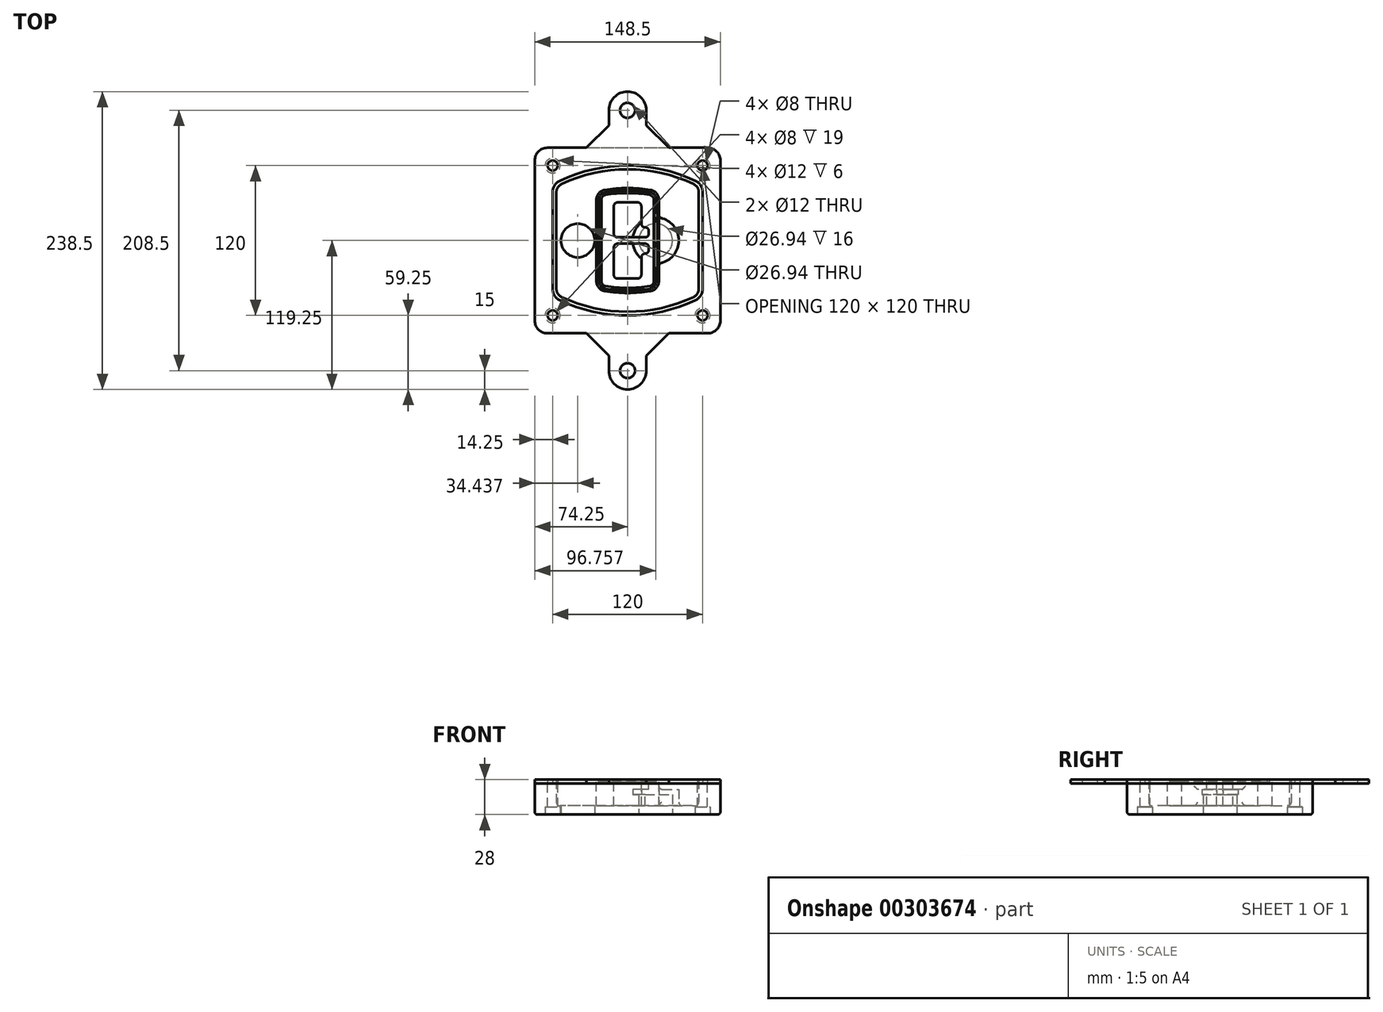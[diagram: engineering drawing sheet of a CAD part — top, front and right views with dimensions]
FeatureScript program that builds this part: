
annotation { "Feature Type Name" : "Feature", "Feature Type Description" : "" }
export const myFeature = defineFeature(function(context is Context, id is Id, definition is map)
    precondition{}
    {
        {
            var Q0;
            Q0=qCreatedBy(makeId("Top.planeOp"),FACE);
            var sketch = newSketch(context, id + "F0", { "sketchPlane" : qUnion([Q0])});
            skPoint(sketch, "E0.rect.middle", {"position": v(0, 0) * mm});
            skLineSegment(sketch, "E1.bottom", {"start": v(-64.25, -74.25) * mm, "end": v(64.25, -74.25) * mm});
            skLineSegment(sketch, "E1.top", {"start": v(-64.25, 74.25) * mm, "end": v(64.25, 74.25) * mm});
            skLineSegment(sketch, "E1.left", {"start": v(-74.25, -64.25) * mm, "end": v(-74.25, 64.25) * mm});
            skLineSegment(sketch, "E1.right", {"start": v(74.25, -64.25) * mm, "end": v(74.25, 64.25) * mm});
            skLineSegment(sketch, "E2", {"start": v(-74.25, 74.25) * mm, "end": v(74.25, -74.25) * mm, "construction": true});
            skLineSegment(sketch, "E3", {"start": v(74.25, 74.25) * mm, "end": v(-74.25, -74.25) * mm, "construction": true});
            skCircle(sketch, "E4", {"center": v(-60, 60) * mm, "radius": 4 * mm});
            skCircle(sketch, "E5", {"center": v(60, 60) * mm, "radius": 4 * mm});
            skCircle(sketch, "E6", {"center": v(60, -60) * mm, "radius": 4 * mm});
            skCircle(sketch, "E7", {"center": v(-60, -60) * mm, "radius": 4 * mm});
            skLineSegment(sketch, "E8", {"start": v(-60, 60) * mm, "end": v(60, 60) * mm, "construction": true});
            skLineSegment(sketch, "E9", {"start": v(60, 60) * mm, "end": v(60, -60) * mm, "construction": true});
            skLineSegment(sketch, "E10", {"start": v(60, -60) * mm, "end": v(-60, -60) * mm, "construction": true});
            skLineSegment(sketch, "E11", {"start": v(-60, -60) * mm, "end": v(-60, 60) * mm, "construction": true});
            skLineSegment(sketch, "E12", {"start": v(-60, 38.83) * mm, "end": v(-60, -38.83) * mm});
            skLineSegment(sketch, "E13", {"start": v(60, 38.83) * mm, "end": v(60, -38.83) * mm});
            skArc(sketch, "E14", {"start": v(54.26, 47.88) * mm, "mid": v(0, 60) * mm, "end": v(-54.26, 47.88) * mm});
            skArc(sketch, "E15", {"start": v(-54.26, -47.88) * mm, "mid": v(0, -60) * mm, "end": v(54.26, -47.88) * mm});
            skLineSegment(sketch, "E16", {"start": v(-60, 0) * mm, "end": v(60, 0) * mm, "construction": true});
            skPoint(sketch, "E17.visualSharp", {"position": v(-60, -45) * mm});
            skArc(sketch, "E17.filletArc", {"start": v(-60, -38.83) * mm, "mid": v(-58.44, -44.2) * mm, "end": v(-54.26, -47.88) * mm});
            skPoint(sketch, "E18.visualSharp", {"position": v(-60, 45) * mm});
            skArc(sketch, "E18.filletArc", {"start": v(-54.26, 47.88) * mm, "mid": v(-58.44, 44.2) * mm, "end": v(-60, 38.83) * mm});
            skPoint(sketch, "E19.visualSharp", {"position": v(60, 45) * mm});
            skArc(sketch, "E19.filletArc", {"start": v(60, 38.83) * mm, "mid": v(58.44, 44.2) * mm, "end": v(54.26, 47.88) * mm});
            skPoint(sketch, "E20.visualSharp", {"position": v(60, -45) * mm});
            skArc(sketch, "E20.filletArc", {"start": v(54.26, -47.88) * mm, "mid": v(58.44, -44.2) * mm, "end": v(60, -38.83) * mm});
            skPoint(sketch, "E21.visualSharp", {"position": v(-74.25, 74.25) * mm});
            skArc(sketch, "E21.filletArc", {"start": v(-64.25, 74.25) * mm, "mid": v(-71.32, 71.32) * mm, "end": v(-74.25, 64.25) * mm});
            skPoint(sketch, "E22.visualSharp", {"position": v(74.25, 74.25) * mm});
            skArc(sketch, "E22.filletArc", {"start": v(74.25, 64.25) * mm, "mid": v(71.32, 71.32) * mm, "end": v(64.25, 74.25) * mm});
            skPoint(sketch, "E23.visualSharp", {"position": v(74.25, -74.25) * mm});
            skArc(sketch, "E23.filletArc", {"start": v(64.25, -74.25) * mm, "mid": v(71.32, -71.32) * mm, "end": v(74.25, -64.25) * mm});
            skPoint(sketch, "E24.visualSharp", {"position": v(-74.25, -74.25) * mm});
            skArc(sketch, "E24.filletArc", {"start": v(-74.25, -64.25) * mm, "mid": v(-71.32, -71.32) * mm, "end": v(-64.25, -74.25) * mm});
            skArc(sketch, "E25.0", {"start": v(57, 38.83) * mm, "mid": v(55.9, 42.58) * mm, "end": v(52.98, 45.17) * mm});
            skLineSegment(sketch, "E25.1", {"start": v(57, 38.83) * mm, "end": v(57, -38.83) * mm});
            skArc(sketch, "E25.2", {"start": v(52.98, -45.17) * mm, "mid": v(55.9, -42.58) * mm, "end": v(57, -38.83) * mm});
            skArc(sketch, "E25.3", {"start": v(-52.98, -45.17) * mm, "mid": v(0, -57) * mm, "end": v(52.98, -45.17) * mm});
            skArc(sketch, "E25.4", {"start": v(-57, -38.83) * mm, "mid": v(-55.9, -42.58) * mm, "end": v(-52.98, -45.17) * mm});
            skArc(sketch, "E25.5", {"start": v(52.98, 45.17) * mm, "mid": v(0, 57) * mm, "end": v(-52.98, 45.17) * mm});
            skLineSegment(sketch, "E25.6", {"start": v(-57, 38.83) * mm, "end": v(-57, -38.83) * mm});
            skArc(sketch, "E25.7", {"start": v(-52.98, 45.17) * mm, "mid": v(-55.9, 42.58) * mm, "end": v(-57, 38.83) * mm});
            skArc(sketch, "E26.0", {"start": v(-55.96, 51.5) * mm, "mid": v(-61.82, 46.33) * mm, "end": v(-64, 38.83) * mm});
            skArc(sketch, "E26.1", {"start": v(55.96, 51.5) * mm, "mid": v(0, 64) * mm, "end": v(-55.96, 51.5) * mm});
            skArc(sketch, "E26.2", {"start": v(64, 38.83) * mm, "mid": v(61.82, 46.33) * mm, "end": v(55.96, 51.5) * mm});
            skLineSegment(sketch, "E26.3", {"start": v(64, 38.83) * mm, "end": v(64, -38.83) * mm});
            skArc(sketch, "E26.4", {"start": v(55.96, -51.5) * mm, "mid": v(61.82, -46.33) * mm, "end": v(64, -38.83) * mm});
            skLineSegment(sketch, "E26.5", {"start": v(-64, 38.83) * mm, "end": v(-64, -38.83) * mm});
            skArc(sketch, "E26.6", {"start": v(-55.96, -51.5) * mm, "mid": v(0, -64) * mm, "end": v(55.96, -51.5) * mm});
            skArc(sketch, "E26.7", {"start": v(-64, -38.83) * mm, "mid": v(-61.82, -46.33) * mm, "end": v(-55.96, -51.5) * mm});
            skSolve(sketch);
        }
        {
            var Q0;
            Q0=makeQuery(id+"F0.imprint","IMPRINT",FACE,{"disambiguationData":[TD([[makeQuery(id+"F0.imprint","IMPRINT",EDGE,{"derivedFrom":sQuery(id+"F0.wireOp",EDGE,"E1.bottom")}),1.0]])]});
            var Q1;
            Q1=makeQuery(id+"F0.imprint","IMPRINT",FACE,{"disambiguationData":[TD([[makeQuery(id+"F0.imprint","IMPRINT",EDGE,{"derivedFrom":sQuery(id+"F0.wireOp",EDGE,"E12")}),1.0]])]});
            var Q2;
            Q2=makeQuery(id+"F0.imprint","IMPRINT",FACE,{"disambiguationData":[TD([[makeQuery(id+"F0.imprint","IMPRINT",EDGE,{"derivedFrom":sQuery(id+"F0.wireOp",EDGE,"E25.0")}),1.0]])]});
            var Q3;
            Q3=makeQuery(id+"F0.imprint","IMPRINT",FACE,{"disambiguationData":[TD([[makeQuery(id+"F0.imprint","IMPRINT",EDGE,{"derivedFrom":sQuery(id+"F0.wireOp",EDGE,"E12")}),-1.0]])]});
            extrude(context, id + "F1", {"entities" : qUnion([Q0, Q1, Q2, Q3]), "oppositeDirection" : true, "depth" : 25 * mm});
        }
        {
            var Q0;
            Q0=makeQuery(id+"F0.imprint","IMPRINT",FACE,{"disambiguationData":[TD([[makeQuery(id+"F0.imprint","IMPRINT",EDGE,{"derivedFrom":sQuery(id+"F0.wireOp",EDGE,"E12")}),1.0]])]});
            extrude(context, id + "F2", {"entities" : qUnion([Q0]), "operationType" : NewBodyOperationType.ADD, "depth" : 3 * mm});
        }
        {
            var Q0;
            Q0=makeQuery(id+"F0.imprint","IMPRINT",FACE,{"disambiguationData":[TD([[makeQuery(id+"F0.imprint","IMPRINT",EDGE,{"derivedFrom":sQuery(id+"F0.wireOp",EDGE,"E25.0")}),1.0]])]});
            extrude(context, id + "F3", {"entities" : qUnion([Q0]), "operationType" : NewBodyOperationType.REMOVE, "oppositeDirection" : true, "depth" : 18 * mm});
        }
        {
            var Q0;
            Q0=makeQuery(id+"F2.opExtrude","CAP_FACE",FACE,{"disambiguationData":[OSD([sQuery(id+"F0.wireOp",EDGE,"E12"),sQuery(id+"F0.wireOp",EDGE,"E13"),sQuery(id+"F0.wireOp",EDGE,"E14"),sQuery(id+"F0.wireOp",EDGE,"E15"),sQuery(id+"F0.wireOp",EDGE,"E17.filletArc"),sQuery(id+"F0.wireOp",EDGE,"E18.filletArc"),sQuery(id+"F0.wireOp",EDGE,"E19.filletArc"),sQuery(id+"F0.wireOp",EDGE,"E20.filletArc"),sQuery(id+"F0.wireOp",EDGE,"E25.0"),sQuery(id+"F0.wireOp",EDGE,"E25.1"),sQuery(id+"F0.wireOp",EDGE,"E25.2"),sQuery(id+"F0.wireOp",EDGE,"E25.3"),sQuery(id+"F0.wireOp",EDGE,"E25.4"),sQuery(id+"F0.wireOp",EDGE,"E25.5"),sQuery(id+"F0.wireOp",EDGE,"E25.6"),sQuery(id+"F0.wireOp",EDGE,"E25.7")])],"isStart":false});
            var sketch = newSketch(context, id + "F4", { "sketchPlane" : qUnion([Q0])});
            skArc(sketch, "E27.0", {"start": v(-18.34, -40.45) * mm, "mid": v(0, -42) * mm, "end": v(18.34, -40.45) * mm});
            skArc(sketch, "E28.0", {"start": v(18.34, 40.45) * mm, "mid": v(0, 42) * mm, "end": v(-18.34, 40.45) * mm});
            skLineSegment(sketch, "E29", {"start": v(-25, 32.57) * mm, "end": v(-25, -32.57) * mm});
            skLineSegment(sketch, "E30", {"start": v(25, 32.57) * mm, "end": v(25, -32.57) * mm});
            skLineSegment(sketch, "E31", {"start": v(-25, 39.1) * mm, "end": v(25, 39.1) * mm, "construction": true});
            skLineSegment(sketch, "E32", {"start": v(-25, -39.1) * mm, "end": v(25, -39.1) * mm, "construction": true});
            skPoint(sketch, "E33.visualSharp", {"position": v(-25, 39.1) * mm});
            skArc(sketch, "E33.filletArc", {"start": v(-18.34, 40.45) * mm, "mid": v(-23.11, 37.73) * mm, "end": v(-25, 32.57) * mm});
            skPoint(sketch, "E34.visualSharp", {"position": v(25, 39.1) * mm});
            skArc(sketch, "E34.filletArc", {"start": v(25, 32.57) * mm, "mid": v(23.11, 37.73) * mm, "end": v(18.34, 40.45) * mm});
            skPoint(sketch, "E35.visualSharp", {"position": v(25, -39.1) * mm});
            skArc(sketch, "E35.filletArc", {"start": v(18.34, -40.45) * mm, "mid": v(23.11, -37.73) * mm, "end": v(25, -32.57) * mm});
            skPoint(sketch, "E36.visualSharp", {"position": v(-25, -39.1) * mm});
            skArc(sketch, "E36.filletArc", {"start": v(-25, -32.57) * mm, "mid": v(-23.11, -37.73) * mm, "end": v(-18.34, -40.45) * mm});
            skArc(sketch, "E37.0", {"start": v(52.98, 45.17) * mm, "mid": v(0, 57) * mm, "end": v(-52.98, 45.17) * mm});
            skArc(sketch, "E37.1", {"start": v(-52.98, 45.17) * mm, "mid": v(-55.9, 42.58) * mm, "end": v(-57, 38.83) * mm});
            skLineSegment(sketch, "E37.2", {"start": v(-57, 38.83) * mm, "end": v(-57, -38.83) * mm});
            skArc(sketch, "E37.3", {"start": v(-57, -38.83) * mm, "mid": v(-55.9, -42.58) * mm, "end": v(-52.98, -45.17) * mm});
            skArc(sketch, "E37.4", {"start": v(-52.98, -45.17) * mm, "mid": v(0, -57) * mm, "end": v(52.98, -45.17) * mm});
            skArc(sketch, "E37.5", {"start": v(52.98, -45.17) * mm, "mid": v(55.9, -42.58) * mm, "end": v(57, -38.83) * mm});
            skLineSegment(sketch, "E37.6", {"start": v(57, 38.83) * mm, "end": v(57, -38.83) * mm});
            skArc(sketch, "E37.7", {"start": v(57, 38.83) * mm, "mid": v(55.9, 42.58) * mm, "end": v(52.98, 45.17) * mm});
            skLineSegment(sketch, "E38.0", {"start": v(23, 32.57) * mm, "end": v(23, -32.57) * mm});
            skArc(sketch, "E38.1", {"start": v(18, -38.48) * mm, "mid": v(21.58, -36.44) * mm, "end": v(23, -32.57) * mm});
            skArc(sketch, "E38.2", {"start": v(-18, -38.48) * mm, "mid": v(0, -40) * mm, "end": v(18, -38.48) * mm});
            skArc(sketch, "E38.3", {"start": v(-23, -32.57) * mm, "mid": v(-21.58, -36.44) * mm, "end": v(-18, -38.48) * mm});
            skLineSegment(sketch, "E38.4", {"start": v(-23, 32.57) * mm, "end": v(-23, -32.57) * mm});
            skArc(sketch, "E38.5", {"start": v(23, 32.57) * mm, "mid": v(21.58, 36.44) * mm, "end": v(18, 38.48) * mm});
            skArc(sketch, "E38.6", {"start": v(-18, 38.48) * mm, "mid": v(-21.58, 36.44) * mm, "end": v(-23, 32.57) * mm});
            skArc(sketch, "E38.7", {"start": v(18, 38.48) * mm, "mid": v(0, 40) * mm, "end": v(-18, 38.48) * mm});
            skArc(sketch, "E39.0", {"start": v(21, 32.57) * mm, "mid": v(20.06, 35.15) * mm, "end": v(17.67, 36.5) * mm});
            skLineSegment(sketch, "E39.1", {"start": v(21, 32.57) * mm, "end": v(21, -32.57) * mm});
            skArc(sketch, "E39.2", {"start": v(17.67, -36.5) * mm, "mid": v(20.06, -35.15) * mm, "end": v(21, -32.57) * mm});
            skArc(sketch, "E39.3", {"start": v(-17.67, -36.5) * mm, "mid": v(0, -38) * mm, "end": v(17.67, -36.5) * mm});
            skArc(sketch, "E39.4", {"start": v(-21, -32.57) * mm, "mid": v(-20.06, -35.15) * mm, "end": v(-17.67, -36.5) * mm});
            skArc(sketch, "E39.5", {"start": v(17.67, 36.5) * mm, "mid": v(0, 38) * mm, "end": v(-17.67, 36.5) * mm});
            skLineSegment(sketch, "E39.6", {"start": v(-21, 32.57) * mm, "end": v(-21, -32.57) * mm});
            skArc(sketch, "E39.7", {"start": v(-17.67, 36.5) * mm, "mid": v(-20.06, 35.15) * mm, "end": v(-21, 32.57) * mm});
            skLineSegment(sketch, "E40", {"start": v(-25, 0) * mm, "end": v(25, 0) * mm, "construction": true});
            skLineSegment(sketch, "E41", {"start": v(-11, 5.5) * mm, "end": v(-11, 27.5) * mm});
            skLineSegment(sketch, "E42", {"start": v(-8, 30.5) * mm, "end": v(8, 30.5) * mm});
            skLineSegment(sketch, "E43", {"start": v(11, 27.5) * mm, "end": v(11, 13.5) * mm});
            skLineSegment(sketch, "E44", {"start": v(14, 10.5) * mm, "end": v(14, 10.5) * mm});
            skLineSegment(sketch, "E45", {"start": v(17, 7.5) * mm, "end": v(17, 5.5) * mm});
            skLineSegment(sketch, "E46", {"start": v(14, 2.5) * mm, "end": v(-8, 2.5) * mm});
            skPoint(sketch, "E47.visualSharp", {"position": v(-11, 30.5) * mm});
            skArc(sketch, "E47.filletArc", {"start": v(-8, 30.5) * mm, "mid": v(-10.12, 29.62) * mm, "end": v(-11, 27.5) * mm});
            skPoint(sketch, "E48.visualSharp", {"position": v(11, 30.5) * mm});
            skArc(sketch, "E48.filletArc", {"start": v(11, 27.5) * mm, "mid": v(10.12, 29.62) * mm, "end": v(8, 30.5) * mm});
            skPoint(sketch, "E49.visualSharp", {"position": v(11, 10.5) * mm});
            skArc(sketch, "E49.filletArc", {"start": v(11, 13.5) * mm, "mid": v(11.88, 11.38) * mm, "end": v(14, 10.5) * mm});
            skPoint(sketch, "E50.visualSharp", {"position": v(17, 10.5) * mm});
            skArc(sketch, "E50.filletArc", {"start": v(17, 7.5) * mm, "mid": v(16.12, 9.62) * mm, "end": v(14, 10.5) * mm});
            skPoint(sketch, "E51.visualSharp", {"position": v(17, 2.5) * mm});
            skArc(sketch, "E51.filletArc", {"start": v(14, 2.5) * mm, "mid": v(16.12, 3.38) * mm, "end": v(17, 5.5) * mm});
            skPoint(sketch, "E52.visualSharp", {"position": v(-11, 2.5) * mm});
            skArc(sketch, "E52.filletArc", {"start": v(-11, 5.5) * mm, "mid": v(-10.12, 3.38) * mm, "end": v(-8, 2.5) * mm});
            skLineSegment(sketch, "E53.0.MirrorCS", {"start": v(14, -2.5) * mm, "end": v(-8, -2.5) * mm});
            skArc(sketch, "E54.0.MirrorCS", {"start": v(-11, -5.5) * mm, "mid": v(-10.12, -3.38) * mm, "end": v(-8, -2.5) * mm});
            skLineSegment(sketch, "E55.0.MirrorCS", {"start": v(-11, -5.5) * mm, "end": v(-11, -27.5) * mm});
            skArc(sketch, "E56.0.MirrorCS", {"start": v(-8, -30.5) * mm, "mid": v(-10.12, -29.62) * mm, "end": v(-11, -27.5) * mm});
            skLineSegment(sketch, "E57.0.MirrorCS", {"start": v(-8, -30.5) * mm, "end": v(8, -30.5) * mm});
            skArc(sketch, "E58.0.MirrorCS", {"start": v(11, -27.5) * mm, "mid": v(10.12, -29.62) * mm, "end": v(8, -30.5) * mm});
            skLineSegment(sketch, "E59.0.MirrorCS", {"start": v(11, -27.5) * mm, "end": v(11, -13.5) * mm});
            skArc(sketch, "E60.0.MirrorCS", {"start": v(11, -13.5) * mm, "mid": v(11.88, -11.38) * mm, "end": v(14, -10.5) * mm});
            skArc(sketch, "E61.0.MirrorCS", {"start": v(17, -7.5) * mm, "mid": v(16.12, -9.62) * mm, "end": v(14, -10.5) * mm});
            skLineSegment(sketch, "E62.0.MirrorCS", {"start": v(17, -7.5) * mm, "end": v(17, -5.5) * mm});
            skArc(sketch, "E63.0.MirrorCS", {"start": v(14, -2.5) * mm, "mid": v(16.12, -3.38) * mm, "end": v(17, -5.5) * mm});
            skSolve(sketch);
        }
        {
            var Q0;
            Q0=makeQuery(id+"F4.imprint","IMPRINT",FACE,{"disambiguationData":[TD([[makeQuery(id+"F4.imprint","IMPRINT",EDGE,{"derivedFrom":sQuery(id+"F4.wireOp",EDGE,"E27.0")}),1.0]])]});
            var Q1;
            Q1=makeQuery(id+"F4.imprint","IMPRINT",FACE,{"disambiguationData":[TD([[makeQuery(id+"F4.imprint","IMPRINT",EDGE,{"derivedFrom":sQuery(id+"F4.wireOp",EDGE,"E38.0")}),-1.0]])]});
            var Q2;
            Q2=makeQuery(id+"F4.imprint","IMPRINT",FACE,{"disambiguationData":[TD([[makeQuery(id+"F4.imprint","IMPRINT",EDGE,{"derivedFrom":sQuery(id+"F4.wireOp",EDGE,"E39.0")}),1.0]])]});
            extrude(context, id + "F5", {"entities" : qUnion([Q0, Q1, Q2]), "operationType" : NewBodyOperationType.ADD, "endBound" : BoundingType.UP_TO_NEXT, "oppositeDirection" : true, "depth" : 25 * mm});
        }
        {
            var Q0;
            Q0=makeQuery(id+"F4.imprint","IMPRINT",FACE,{"disambiguationData":[TD([[makeQuery(id+"F4.imprint","IMPRINT",EDGE,{"derivedFrom":sQuery(id+"F4.wireOp",EDGE,"E38.0")}),-1.0]])]});
            extrude(context, id + "F6", {"entities" : qUnion([Q0]), "operationType" : NewBodyOperationType.REMOVE, "oppositeDirection" : true, "depth" : 2 * mm});
        }
        {
            var Q0;
            Q0=makeQuery(id+"F1.opExtrude","CAP_FACE",FACE,{"disambiguationData":[OSD([sQuery(id+"F0.wireOp",EDGE,"E1.bottom"),sQuery(id+"F0.wireOp",EDGE,"E1.top"),sQuery(id+"F0.wireOp",EDGE,"E1.left"),sQuery(id+"F0.wireOp",EDGE,"E1.right"),sQuery(id+"F0.wireOp",EDGE,"E4"),sQuery(id+"F0.wireOp",EDGE,"E5"),sQuery(id+"F0.wireOp",EDGE,"E6"),sQuery(id+"F0.wireOp",EDGE,"E7"),sQuery(id+"F0.wireOp",EDGE,"E21.filletArc"),sQuery(id+"F0.wireOp",EDGE,"E22.filletArc"),sQuery(id+"F0.wireOp",EDGE,"E23.filletArc"),sQuery(id+"F0.wireOp",EDGE,"E24.filletArc")])],"isStart":false});
            var sketch = newSketch(context, id + "F7", { "sketchPlane" : qUnion([Q0])});
            skCircle(sketch, "E64", {"center": v(22.5, 0) * mm, "radius": 13.47 * mm});
            skCircle(sketch, "E65", {"center": v(-39.81, 0) * mm, "radius": 13.47 * mm});
            skLineSegment(sketch, "E66", {"start": v(74.25, 0) * mm, "end": v(-74.25, 0) * mm});
            skCircle(sketch, "E67", {"center": v(22.5, 0) * mm, "radius": 18.47 * mm});
            skCircle(sketch, "E68", {"center": v(60, -60) * mm, "radius": 6 * mm});
            skCircle(sketch, "E69", {"center": v(-60, -60) * mm, "radius": 6 * mm});
            skCircle(sketch, "E70", {"center": v(-60, 60) * mm, "radius": 6 * mm});
            skCircle(sketch, "E71", {"center": v(60, 60) * mm, "radius": 6 * mm});
            skSolve(sketch);
        }
        {
            var Q0;
            {var subQ1=sQuery(id+"F7.wireOp",EDGE,"E66");var subQ4=sQuery(id+"F7.wireOp",EDGE,"E64");var subQ6=makeQuery(id+"F7.imprint","INTERSECT",VERTEX,{"disambiguationData":[OD(0.0)],"derivedFrom":[subQ4,subQ1]});Q0=makeQuery(id+"F7.imprint","IMPRINT",FACE,{"disambiguationData":[TD([[makeQuery(id+"F7.imprint","IMPRINT",EDGE,{"disambiguationData":[TD([[subQ6,-1.0]])],"derivedFrom":subQ4}),-1.0]])]});}
            var Q1;
            {var subQ0=sQuery(id+"F7.wireOp",EDGE,"E66");var subQ1=sQuery(id+"F7.wireOp",EDGE,"E64");var subQ3=makeQuery(id+"F7.imprint","INTERSECT",VERTEX,{"disambiguationData":[OD(0.0)],"derivedFrom":[subQ1,subQ0]});Q1=makeQuery(id+"F7.imprint","IMPRINT",FACE,{"disambiguationData":[TD([[makeQuery(id+"F7.imprint","IMPRINT",EDGE,{"disambiguationData":[TD([[subQ3,-1.0]])],"derivedFrom":subQ1}),1.0]])]});}
            var Q2;
            {var subQ0=sQuery(id+"F7.wireOp",EDGE,"E66");var subQ1=sQuery(id+"F7.wireOp",EDGE,"E64");var subQ3=makeQuery(id+"F7.imprint","INTERSECT",VERTEX,{"disambiguationData":[OD(0.0)],"derivedFrom":[subQ1,subQ0]});Q2=makeQuery(id+"F7.imprint","IMPRINT",FACE,{"disambiguationData":[TD([[makeQuery(id+"F7.imprint","IMPRINT",EDGE,{"disambiguationData":[TD([[subQ3,1.0]])],"derivedFrom":subQ1}),1.0]])]});}
            var Q3;
            {var subQ1=sQuery(id+"F7.wireOp",EDGE,"E66");var subQ4=sQuery(id+"F7.wireOp",EDGE,"E64");var subQ6=makeQuery(id+"F7.imprint","INTERSECT",VERTEX,{"disambiguationData":[OD(0.0)],"derivedFrom":[subQ4,subQ1]});Q3=makeQuery(id+"F7.imprint","IMPRINT",FACE,{"disambiguationData":[TD([[makeQuery(id+"F7.imprint","IMPRINT",EDGE,{"disambiguationData":[TD([[subQ6,1.0]])],"derivedFrom":subQ4}),-1.0]])]});}
            extrude(context, id + "F8", {"entities" : qUnion([Q0, Q1, Q2, Q3]), "operationType" : NewBodyOperationType.ADD, "oppositeDirection" : true, "depth" : 20 * mm});
        }
        {
            var Q0;
            {var subQ0=sQuery(id+"F7.wireOp",EDGE,"E66");var subQ1=sQuery(id+"F7.wireOp",EDGE,"E64");var subQ3=makeQuery(id+"F7.imprint","INTERSECT",VERTEX,{"disambiguationData":[OD(0.0)],"derivedFrom":[subQ1,subQ0]});Q0=makeQuery(id+"F7.imprint","IMPRINT",FACE,{"disambiguationData":[TD([[makeQuery(id+"F7.imprint","IMPRINT",EDGE,{"disambiguationData":[TD([[subQ3,-1.0]])],"derivedFrom":subQ1}),1.0]])]});}
            var Q1;
            {var subQ0=sQuery(id+"F7.wireOp",EDGE,"E66");var subQ1=sQuery(id+"F7.wireOp",EDGE,"E64");var subQ3=makeQuery(id+"F7.imprint","INTERSECT",VERTEX,{"disambiguationData":[OD(0.0)],"derivedFrom":[subQ1,subQ0]});Q1=makeQuery(id+"F7.imprint","IMPRINT",FACE,{"disambiguationData":[TD([[makeQuery(id+"F7.imprint","IMPRINT",EDGE,{"disambiguationData":[TD([[subQ3,1.0]])],"derivedFrom":subQ1}),1.0]])]});}
            extrude(context, id + "F9", {"entities" : qUnion([Q0, Q1]), "operationType" : NewBodyOperationType.REMOVE, "oppositeDirection" : true, "depth" : 16 * mm});
        }
        {
            var Q0;
            {var subQ0=sQuery(id+"F7.wireOp",EDGE,"E66");var subQ1=sQuery(id+"F7.wireOp",EDGE,"E65");var subQ3=makeQuery(id+"F7.imprint","INTERSECT",VERTEX,{"disambiguationData":[OD(0.0)],"derivedFrom":[subQ1,subQ0]});Q0=makeQuery(id+"F7.imprint","IMPRINT",FACE,{"disambiguationData":[TD([[makeQuery(id+"F7.imprint","IMPRINT",EDGE,{"disambiguationData":[TD([[subQ3,-1.0]])],"derivedFrom":subQ1}),1.0]])]});}
            var Q1;
            {var subQ0=sQuery(id+"F7.wireOp",EDGE,"E66");var subQ1=sQuery(id+"F7.wireOp",EDGE,"E65");var subQ3=makeQuery(id+"F7.imprint","INTERSECT",VERTEX,{"disambiguationData":[OD(0.0)],"derivedFrom":[subQ1,subQ0]});Q1=makeQuery(id+"F7.imprint","IMPRINT",FACE,{"disambiguationData":[TD([[makeQuery(id+"F7.imprint","IMPRINT",EDGE,{"disambiguationData":[TD([[subQ3,1.0]])],"derivedFrom":subQ1}),1.0]])]});}
            extrude(context, id + "F10", {"entities" : qUnion([Q0, Q1]), "operationType" : NewBodyOperationType.REMOVE, "oppositeDirection" : true, "depth" : 25 * mm});
        }
        {
            var Q0;
            Q0=makeQuery(id+"F7.imprint","IMPRINT",FACE,{"disambiguationData":[TD([[makeQuery(id+"F7.imprint","IMPRINT",EDGE,{"derivedFrom":sQuery(id+"F7.wireOp",EDGE,"E68")}),1.0]])]});
            var Q1;
            Q1=makeQuery(id+"F7.imprint","IMPRINT",FACE,{"disambiguationData":[TD([[makeQuery(id+"F7.imprint","IMPRINT",EDGE,{"derivedFrom":makeQuery(id+"F1.opExtrude","CAP_EDGE",EDGE,{"disambiguationData":[OSD([sQuery(id+"F0.wireOp",EDGE,"E5")])],"isStart":false})}),-1.0]])]});
            var Q2;
            Q2=makeQuery(id+"F7.imprint","IMPRINT",FACE,{"disambiguationData":[TD([[makeQuery(id+"F7.imprint","IMPRINT",EDGE,{"derivedFrom":sQuery(id+"F7.wireOp",EDGE,"E69")}),1.0]])]});
            var Q3;
            Q3=makeQuery(id+"F7.imprint","IMPRINT",FACE,{"disambiguationData":[TD([[makeQuery(id+"F7.imprint","IMPRINT",EDGE,{"derivedFrom":makeQuery(id+"F1.opExtrude","CAP_EDGE",EDGE,{"disambiguationData":[OSD([sQuery(id+"F0.wireOp",EDGE,"E4")])],"isStart":false})}),-1.0]])]});
            var Q4;
            Q4=makeQuery(id+"F7.imprint","IMPRINT",FACE,{"disambiguationData":[TD([[makeQuery(id+"F7.imprint","IMPRINT",EDGE,{"derivedFrom":sQuery(id+"F7.wireOp",EDGE,"E70")}),1.0]])]});
            var Q5;
            Q5=makeQuery(id+"F7.imprint","IMPRINT",FACE,{"disambiguationData":[TD([[makeQuery(id+"F7.imprint","IMPRINT",EDGE,{"derivedFrom":makeQuery(id+"F1.opExtrude","CAP_EDGE",EDGE,{"disambiguationData":[OSD([sQuery(id+"F0.wireOp",EDGE,"E7")])],"isStart":false})}),-1.0]])]});
            var Q6;
            Q6=makeQuery(id+"F7.imprint","IMPRINT",FACE,{"disambiguationData":[TD([[makeQuery(id+"F7.imprint","IMPRINT",EDGE,{"derivedFrom":sQuery(id+"F7.wireOp",EDGE,"E71")}),1.0]])]});
            var Q7;
            Q7=makeQuery(id+"F7.imprint","IMPRINT",FACE,{"disambiguationData":[TD([[makeQuery(id+"F7.imprint","IMPRINT",EDGE,{"derivedFrom":makeQuery(id+"F1.opExtrude","CAP_EDGE",EDGE,{"disambiguationData":[OSD([sQuery(id+"F0.wireOp",EDGE,"E6")])],"isStart":false})}),-1.0]])]});
            extrude(context, id + "F11", {"entities" : qUnion([Q0, Q1, Q2, Q3, Q4, Q5, Q6, Q7]), "operationType" : NewBodyOperationType.REMOVE, "oppositeDirection" : true, "depth" : 6 * mm});
        }
        {
            var Q0;
            Q0=makeQuery(id+"F9.boolean.opBoolean","COPY",FACE,{"derivedFrom":makeQuery(id+"F9.opExtrude","CAP_FACE",FACE,{"disambiguationData":[OSD([sQuery(id+"F7.wireOp",EDGE,"E64")])],"isStart":false})});
            var sketch = newSketch(context, id + "F12", { "sketchPlane" : qUnion([Q0])});
            skArc(sketch, "E72.0", {"start": v(11, 14.45) * mm, "mid": v(6.45, 9.13) * mm, "end": v(4.2, 2.5) * mm});
            skArc(sketch, "E72.1", {"start": v(4.2, -2.5) * mm, "mid": v(6.45, -9.13) * mm, "end": v(11, -14.45) * mm});
            skLineSegment(sketch, "E73", {"start": v(4.2, -2.5) * mm, "end": v(14, -2.5) * mm});
            skLineSegment(sketch, "E74.0", {"start": v(14, 2.5) * mm, "end": v(4.2, 2.5) * mm});
            skArc(sketch, "E74.1", {"start": v(14, 2.5) * mm, "mid": v(16.12, 3.38) * mm, "end": v(17, 5.5) * mm});
            skLineSegment(sketch, "E74.2", {"start": v(17, 7.5) * mm, "end": v(17, 5.5) * mm});
            skArc(sketch, "E74.3", {"start": v(17, 7.5) * mm, "mid": v(16.12, 9.62) * mm, "end": v(14, 10.5) * mm});
            skArc(sketch, "E74.4", {"start": v(11, 13.5) * mm, "mid": v(11.88, 11.38) * mm, "end": v(14, 10.5) * mm});
            skLineSegment(sketch, "E74.5", {"start": v(11, 14.45) * mm, "end": v(11, 13.5) * mm});
            skLineSegment(sketch, "E74.7", {"start": v(14, -2.5) * mm, "end": v(4.2, -2.5) * mm});
            skArc(sketch, "E74.8", {"start": v(14, -2.5) * mm, "mid": v(16.12, -3.38) * mm, "end": v(17, -5.5) * mm});
            skLineSegment(sketch, "E74.9", {"start": v(17, -7.5) * mm, "end": v(17, -5.5) * mm});
            skArc(sketch, "E74.10", {"start": v(17, -7.5) * mm, "mid": v(16.12, -9.62) * mm, "end": v(14, -10.5) * mm});
            skArc(sketch, "E74.11", {"start": v(11, -13.5) * mm, "mid": v(11.88, -11.38) * mm, "end": v(14, -10.5) * mm});
            skLineSegment(sketch, "E74.12", {"start": v(11, -14.45) * mm, "end": v(11, -13.5) * mm});
            skPoint(sketch, "E75.orphan", {"position": v(11, -27.5) * mm});
            skPoint(sketch, "E76.orphan", {"position": v(-8, -2.5) * mm});
            skPoint(sketch, "E77.orphan", {"position": v(-8, 2.5) * mm});
            skPoint(sketch, "E78.orphan", {"position": v(11, 27.5) * mm});
            skSolve(sketch);
        }
        {
            var Q0;
            {var subQ7=sQuery(id+"F12.wireOp",EDGE,"E72.0");var subQ14=sQuery(id+"F12.wireOp",EDGE,"E72.1");var subQ16=sQuery(id+"F12.wireOp",EDGE,"E74.1");var subQ18=sQuery(id+"F12.wireOp",EDGE,"E74.8");Q0=qUnion([makeQuery(id+"F12.imprint","IMPRINT",FACE,{"disambiguationData":[TD([[makeQuery(id+"F12.imprint","IMPRINT",EDGE,{"derivedFrom":subQ7}),1.0]])]}),makeQuery(id+"F12.imprint","IMPRINT",FACE,{"disambiguationData":[TD([[makeQuery(id+"F12.imprint","IMPRINT",EDGE,{"derivedFrom":subQ14}),1.0]])]}),makeQuery(id+"F12.imprint","IMPRINT",FACE,{"disambiguationData":[TD([[makeQuery(id+"F12.imprint","IMPRINT",EDGE,{"derivedFrom":subQ16}),1.0]])]}),makeQuery(id+"F12.imprint","IMPRINT",FACE,{"disambiguationData":[TD([[makeQuery(id+"F12.imprint","IMPRINT",EDGE,{"derivedFrom":subQ18}),-1.0]])]})]);}
            var Q1;
            Q1=makeQuery(id+"F5.boolean.opBoolean","SPLIT",FACE,{"disambiguationData":[TD([makeQuery(id+"F5.opExtrude","SWEPT_FACE",FACE,{"disambiguationData":[OSD([sQuery(id+"F4.wireOp",EDGE,"E41")])]})])],"derivedFrom":makeQuery(id+"F3.boolean.opBoolean","COPY",FACE,{"derivedFrom":makeQuery(id+"F3.opExtrude","CAP_FACE",FACE,{"disambiguationData":[OSD([sQuery(id+"F0.wireOp",EDGE,"E25.0"),sQuery(id+"F0.wireOp",EDGE,"E25.1"),sQuery(id+"F0.wireOp",EDGE,"E25.2"),sQuery(id+"F0.wireOp",EDGE,"E25.3"),sQuery(id+"F0.wireOp",EDGE,"E25.4"),sQuery(id+"F0.wireOp",EDGE,"E25.5"),sQuery(id+"F0.wireOp",EDGE,"E25.6"),sQuery(id+"F0.wireOp",EDGE,"E25.7")])],"isStart":false})})});
            extrude(context, id + "F13", {"entities" : qUnion([Q0]), "operationType" : NewBodyOperationType.REMOVE, "endBound" : BoundingType.UP_TO_SURFACE, "endBoundEntityFace" : qUnion([Q1]), "depth" : 25 * mm});
        }
        {
            var Q0;
            Q0=makeQuery(id+"F3.boolean.opBoolean","COPY",EDGE,{"derivedFrom":makeQuery(id+"F3.opExtrude","CAP_EDGE",EDGE,{"disambiguationData":[OSD([sQuery(id+"F0.wireOp",EDGE,"E25.6")])],"isStart":false})});
            var Q1;
            Q1=makeQuery(id+"F8.boolean.opBoolean","INTERSECT",EDGE,{"derivedFrom":[makeQuery(id+"F5.opExtrude","SWEPT_FACE",FACE,{"disambiguationData":[OSD([sQuery(id+"F4.wireOp",EDGE,"E30")])]}),makeQuery(id+"F8.opExtrude","CAP_FACE",FACE,{"disambiguationData":[OSD([sQuery(id+"F7.wireOp",EDGE,"E67")])],"isStart":false})]});
            var Q2;
            Q2=makeQuery(id+"F8.boolean.opBoolean","INTERSECT",EDGE,{"disambiguationData":[OD(1.0)],"derivedFrom":[makeQuery(id+"F5.opExtrude","SWEPT_FACE",FACE,{"disambiguationData":[OSD([sQuery(id+"F4.wireOp",EDGE,"E30")])]}),makeQuery(id+"F8.opExtrude","SWEPT_FACE",FACE,{"disambiguationData":[OSD([sQuery(id+"F7.wireOp",EDGE,"E67")])]})]});
            var Q3;
            {var subQ0=sQuery(id+"F4.wireOp",EDGE,"E30");Q3=makeQuery(id+"F8.boolean.opBoolean","SPLIT",EDGE,{"disambiguationData":[TD([makeQuery(id+"F5.opExtrude","SWEPT_FACE",FACE,{"disambiguationData":[OSD([sQuery(id+"F4.wireOp",EDGE,"E35.filletArc")])]})])],"derivedFrom":makeQuery(id+"F5.opExtrude","CAP_EDGE",EDGE,{"disambiguationData":[OSD([subQ0])],"isStart":false})});}
            var Q4;
            {var subQ0=sQuery(id+"F0.wireOp",EDGE,"E25.7");var subQ1=sQuery(id+"F0.wireOp",EDGE,"E25.1");var subQ2=sQuery(id+"F0.wireOp",EDGE,"E25.6");var subQ3=sQuery(id+"F0.wireOp",EDGE,"E25.5");var subQ4=sQuery(id+"F0.wireOp",EDGE,"E25.4");var subQ5=sQuery(id+"F0.wireOp",EDGE,"E25.0");var subQ6=sQuery(id+"F0.wireOp",EDGE,"E25.2");var subQ7=sQuery(id+"F0.wireOp",EDGE,"E25.3");Q4=makeQuery(id+"F8.boolean.opBoolean","INTERSECT",EDGE,{"derivedFrom":[makeQuery(id+"F5.boolean.opBoolean","SPLIT",FACE,{"disambiguationData":[TD([makeQuery(id+"F2.opExtrude","SWEPT_FACE",FACE,{"disambiguationData":[OSD([subQ5])]})])],"derivedFrom":makeQuery(id+"F3.boolean.opBoolean","COPY",FACE,{"derivedFrom":makeQuery(id+"F3.opExtrude","CAP_FACE",FACE,{"disambiguationData":[OSD([subQ5,subQ1,subQ6,subQ7,subQ4,subQ3,subQ2,subQ0])],"isStart":false})})}),makeQuery(id+"F8.opExtrude","SWEPT_FACE",FACE,{"disambiguationData":[OSD([sQuery(id+"F7.wireOp",EDGE,"E67")])]})]});}
            var Q5;
            Q5=makeQuery(id+"F8.boolean.opBoolean","INTERSECT",EDGE,{"disambiguationData":[OD(0.0)],"derivedFrom":[makeQuery(id+"F5.opExtrude","SWEPT_FACE",FACE,{"disambiguationData":[OSD([sQuery(id+"F4.wireOp",EDGE,"E30")])]}),makeQuery(id+"F8.opExtrude","SWEPT_FACE",FACE,{"disambiguationData":[OSD([sQuery(id+"F7.wireOp",EDGE,"E67")])]})]});
            fillet(context, id + "F14", {"entities" : qUnion([Q0, Q1, Q2, Q3, Q4, Q5]), "radius" : 3 * mm, "tangentPropagation" : true, "allowEdgeOverflow" : false});
        }
        {
            var Q0;
            Q0=makeQuery(id+"F1.opExtrude","CAP_EDGE",EDGE,{"disambiguationData":[OSD([sQuery(id+"F0.wireOp",EDGE,"E1.bottom")])],"isStart":false});
            fillet(context, id + "F15", {"entities" : qUnion([Q0]), "radius" : 2 * mm, "tangentPropagation" : true, "allowEdgeOverflow" : false});
        }
        {
            var Q0;
            {var subQ0=sQuery(id+"F0.wireOp",EDGE,"E21.filletArc");var subQ1=sQuery(id+"F0.wireOp",EDGE,"E7");var subQ2=sQuery(id+"F0.wireOp",EDGE,"E6");var subQ3=sQuery(id+"F0.wireOp",EDGE,"E5");var subQ4=sQuery(id+"F0.wireOp",EDGE,"E4");var subQ5=sQuery(id+"F0.wireOp",EDGE,"E22.filletArc");var subQ6=sQuery(id+"F0.wireOp",EDGE,"E1.bottom");var subQ7=sQuery(id+"F0.wireOp",EDGE,"E1.right");var subQ8=sQuery(id+"F0.wireOp",EDGE,"E1.top");var subQ9=sQuery(id+"F0.wireOp",EDGE,"E1.left");var subQ10=sQuery(id+"F0.wireOp",EDGE,"E23.filletArc");var subQ11=sQuery(id+"F0.wireOp",EDGE,"E24.filletArc");Q0=makeQuery(id+"F2.boolean.opBoolean","SPLIT",FACE,{"disambiguationData":[TD([makeQuery(id+"F1.opExtrude","SWEPT_FACE",FACE,{"disambiguationData":[OSD([subQ6])]})])],"derivedFrom":makeQuery(id+"F1.opExtrude","CAP_FACE",FACE,{"disambiguationData":[OSD([subQ6,subQ8,subQ9,subQ7,subQ4,subQ3,subQ2,subQ1,subQ0,subQ5,subQ10,subQ11])],"isStart":true})});}
            var sketch = newSketch(context, id + "F16", { "sketchPlane" : qUnion([Q0])});
            skPoint(sketch, "E79.endSnap0", {"position": v(0, 74.25) * mm});
            skLineSegment(sketch, "E80", {"start": v(0, 0) * mm, "end": v(0, 104.25) * mm, "construction": true});
            skPoint(sketch, "E80.endSnap0", {"position": v(0, 60) * mm});
            skCircle(sketch, "E81", {"center": v(0, 104.25) * mm, "radius": 6 * mm});
            skArc(sketch, "E82", {"start": v(15, 104.25) * mm, "mid": v(0, 119.25) * mm, "end": v(-15, 104.25) * mm});
            skLineSegment(sketch, "E83", {"start": v(-15, 92.25) * mm, "end": v(-33, 74.25) * mm});
            skLineSegment(sketch, "E84", {"start": v(15, 104.25) * mm, "end": v(15, 92.25) * mm});
            skLineSegment(sketch, "E85", {"start": v(15, 92.25) * mm, "end": v(33, 74.25) * mm});
            skPoint(sketch, "E86.endSnap0", {"position": v(74.25, 0) * mm});
            skArc(sketch, "E87.MirrorCS", {"start": v(15, -104.25) * mm, "mid": v(0, -119.25) * mm, "end": v(-15, -104.25) * mm});
            skLineSegment(sketch, "E88.MirrorCS", {"start": v(15, -104.25) * mm, "end": v(15, -92.25) * mm});
            skCircle(sketch, "E89.MirrorC", {"center": v(0, -104.25) * mm, "radius": 6 * mm});
            skLineSegment(sketch, "E90.MirrorCS", {"start": v(0, 0) * mm, "end": v(0, -104.25) * mm, "construction": true});
            skLineSegment(sketch, "E91.MirrorCS", {"start": v(15, -92.25) * mm, "end": v(33, -74.25) * mm});
            skLineSegment(sketch, "E92.MirrorCS", {"start": v(-15, -104.25) * mm, "end": v(-15, -92.25) * mm});
            skLineSegment(sketch, "E93.MirrorCS", {"start": v(-15, -92.25) * mm, "end": v(-33, -74.25) * mm});
            skPoint(sketch, "E94.MirrorP", {"position": v(0, -74.25) * mm});
            skLineSegment(sketch, "E95", {"start": v(74.25, 0) * mm, "end": v(-74.25, 0) * mm, "construction": true});
            skLineSegment(sketch, "E96", {"start": v(-15, 104.25) * mm, "end": v(-15, 92.25) * mm});
            skSolve(sketch);
        }
        {
            var Q0;
            Q0=makeQuery(id+"F16.imprint","IMPRINT",FACE,{"disambiguationData":[TD([[makeQuery(id+"F16.imprint","IMPRINT",EDGE,{"derivedFrom":sQuery(id+"F16.wireOp",EDGE,"E81")}),-1.0]])]});
            var Q1;
            Q1=makeQuery(id+"F16.imprint","IMPRINT",FACE,{"disambiguationData":[TD([[makeQuery(id+"F16.imprint","IMPRINT",EDGE,{"derivedFrom":makeQuery(id+"F1.opExtrude","CAP_EDGE",EDGE,{"disambiguationData":[OSD([sQuery(id+"F0.wireOp",EDGE,"E1.left")])],"isStart":true})}),-1.0]])]});
            var Q2;
            Q2=makeQuery(id+"F16.imprint","IMPRINT",FACE,{"disambiguationData":[TD([[makeQuery(id+"F16.imprint","IMPRINT",EDGE,{"derivedFrom":sQuery(id+"F16.wireOp",EDGE,"E92.MirrorCS")}),-1.0]])]});
            var Q3;
            Q3=makeQuery(id+"F2.opExtrude","CAP_FACE",FACE,{"disambiguationData":[OSD([sQuery(id+"F0.wireOp",EDGE,"E12"),sQuery(id+"F0.wireOp",EDGE,"E13"),sQuery(id+"F0.wireOp",EDGE,"E14"),sQuery(id+"F0.wireOp",EDGE,"E15"),sQuery(id+"F0.wireOp",EDGE,"E17.filletArc"),sQuery(id+"F0.wireOp",EDGE,"E18.filletArc"),sQuery(id+"F0.wireOp",EDGE,"E19.filletArc"),sQuery(id+"F0.wireOp",EDGE,"E20.filletArc"),sQuery(id+"F0.wireOp",EDGE,"E25.0"),sQuery(id+"F0.wireOp",EDGE,"E25.1"),sQuery(id+"F0.wireOp",EDGE,"E25.2"),sQuery(id+"F0.wireOp",EDGE,"E25.3"),sQuery(id+"F0.wireOp",EDGE,"E25.4"),sQuery(id+"F0.wireOp",EDGE,"E25.5"),sQuery(id+"F0.wireOp",EDGE,"E25.6"),sQuery(id+"F0.wireOp",EDGE,"E25.7")])],"isStart":false});
            extrude(context, id + "F17", {"entities" : qUnion([Q0, Q1, Q2]), "endBound" : BoundingType.UP_TO_SURFACE, "endBoundEntityFace" : qUnion([Q3]), "depth" : 25 * mm});
        }
    });
